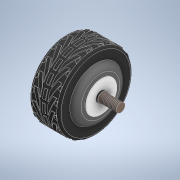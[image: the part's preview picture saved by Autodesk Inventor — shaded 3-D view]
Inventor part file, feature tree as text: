
AUTODESK INVENTOR PART (.ipt)
format: ipt  version: 2021 (Build 250183000, 183)  size: 703,488 bytes
history: native  units: in
note: dims shown in document units (in); Inventor stores cm internally (conversion verified against a paired STEP export)
features: other x3, thread x1, sketch x1
ambient origin geometry x8: Origin, YZ Plane, XZ Plane, XY Plane, X Axis, Y Axis, Z Axis, Center Point
bodies: Body1 (feature_tree)
feature tree (5):
  other  "Sólido2"
  other  "Geometría reparada1"
  thread  "Rosca1"  [1 undecoded]
  sketch  "Boceto6"
  other  "Sólido1"
note: 1 required parameter value undecoded (feature->parameter linkage not recoverable at this tier; creation-order binding heuristic only, values carry confidence <= 0.55)
